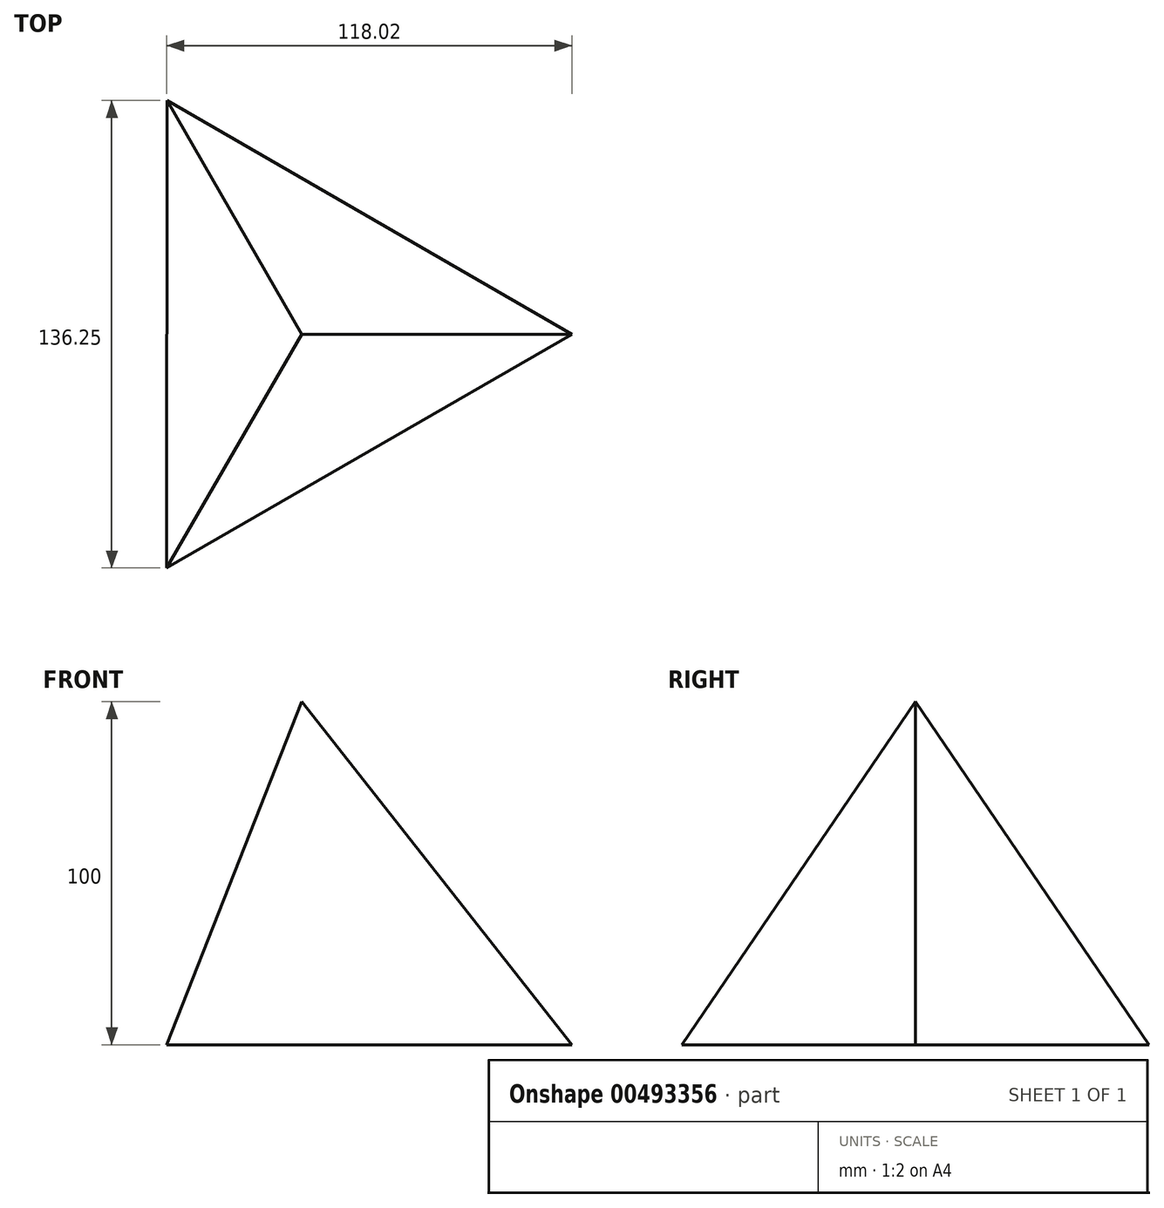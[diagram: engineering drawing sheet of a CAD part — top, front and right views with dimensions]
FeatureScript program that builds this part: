
annotation { "Feature Type Name" : "Feature", "Feature Type Description" : "" }
export const myFeature = defineFeature(function(context is Context, id is Id, definition is map)
    precondition{}
    {
        {
            var Q0;
            Q0=qCreatedBy(makeId("Top.planeOp"),FACE);
            var sketch = newSketch(context, id + "F0", { "sketchPlane" : qUnion([Q0])});
            skCircle(sketch, "E0.cCircle", {"center": v(0, 0) * mm, "radius": 78.66 * mm, "construction": true});
            skLineSegment(sketch, "E0.0", {"start": v(-39.3, 68.14) * mm, "end": v(78.66, -0.03) * mm});
            skLineSegment(sketch, "E0.1", {"start": v(78.66, -0.03) * mm, "end": v(-39.36, -68.1) * mm});
            skLineSegment(sketch, "E0.2", {"start": v(-39.36, -68.1) * mm, "end": v(-39.3, 68.14) * mm});
            skSolve(sketch);
        }
        {
            var Q0;
            Q0=qCreatedBy(makeId("Top.planeOp"),FACE);
            cPlane(context, id + "F1", {"entities" : qUnion([Q0]), "cplaneType" : CPlaneType.OFFSET, "offset" : 100 * mm, "width" : 150 * mm, "height" : 150 * mm});
        }
        {
            var Q0;
            Q0=qCreatedBy(id+"F1.planeOp",FACE);
            var sketch = newSketch(context, id + "F2", { "sketchPlane" : qUnion([Q0])});
            skPoint(sketch, "E1", {"position": v(0, 0) * mm});
            skSolve(sketch);
        }
        {
            var Q0;
            Q0=makeQuery(id+"F0.imprint","IMPRINT",FACE,{"disambiguationData":[TD([[makeQuery(id+"F0.imprint","IMPRINT",EDGE,{"derivedFrom":sQuery(id+"F0.wireOp",EDGE,"E0.0")}),-1.0]])]});
            var Q1;
            Q1=sQuery(id+"F2.wireOp",VERTEX,"E1");
            loft(context, id + "F3", {"sheetProfilesArray" : [{ "sheetProfileEntities" : qUnion([Q0]) }, { "sheetProfileEntities" : qUnion([Q1]) }]});
        }
    });
